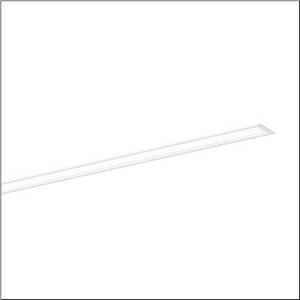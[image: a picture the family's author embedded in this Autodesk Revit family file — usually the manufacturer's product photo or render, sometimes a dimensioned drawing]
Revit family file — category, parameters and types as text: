
# Revit family: silica_r__21_51mx13tbt5w_c30f
name_source: partatom
category: Lighting Fixtures
units: mm (PartAtom-declared; Revit-internal decimal feet)

## family parameters
Cut with Voids When Loaded = No
Host = Face
Light Source = No
Part Type = Normal
Room Calculation Point = No
Round Connector Dimension = Use Diameter
Shared = No

## types (1)
- --- (1 x LED, 4030 lm, 40.5 W, 6500K)
    Apparent Load = 41 VA
    CIE Flux Codes = 78 96 99 100 100
    Color Rendering = 80
    Color Temperature = 6500K
    Default Elevation = 1800 mm
    Description = Silica® 21, office luminaire, primary optical cover: prismatic diffuser, of PMMA, CAT 2 (L<= 3000cd/m²), light emission: direct distribution, primary light characteristic: symmetric, installation type: recessed, LED, rated luminous flux: 4.030lm, luminous efficacy: 95lm/W, light colour: 8tw, colour temperature: 2700..6500K, with terminal, 3+2-pole, max. 2.5mm², mains connection: 220..240V, AC, 50/60Hz, rated input power: 42.6W, luminaire housing, of aluminium, traffic white (RAL 9016), length: 1.528mm, width: 79mm, height: 53mm, protection rating (complete): IP20, insulation class (complete): insulation class I (protective earthing), certification: CE, permissible operating ambient temperature: 0..+35°C, standard: EN 50419, packaging unit: 1 piece
    Height = 0 mm  [stored 0 ft]
    Lamp = 1 x LED
    Lamp Light Flux = 4030 lm
    Lamp Power = 40.5 W
    Lamp count = 1
    Length = 1527 mm
    Luminous efficacy = 100 lm/W
    Manufacturer = Siteco
    ModVariant = No
    Model = 51MX13TBT5W
    Mounting Place = Ceiling
    Mounting Type = Recessed
    Number of Poles = 1
    OnlyDefault = Yes
    Power Factor = 1
    Product Name = Silica® 21
    Product group = office luminaire | ceiling recessed
    ProductGroupID = 400
    Protection Class = Protection class I
    Protection Degree = IP 20
    RLX_Detail_Level = 1
    RlxData = <blob elided: 13037 chars, md5=ea1c272a>
    Socket = socket
    Standby Power = 0 W
    System Light Flux = 4030 lm
    System Power = 41 W
    Type Comments = individual setting
    Type Image = l_1251708.jpg
    URL = http://relux.com
    VarID = @adj_045939
    Voltage = 0 V
    Weight = 0.00 kg
    Width = 79 mm

note: [stored X ft] marks values corroborated as IEEE doubles in the binary element streams (Revit-internal decimal feet)

## geometry (parser evidence)
native form markers: Sweep x9
no freeform markers — native parametric forms only
